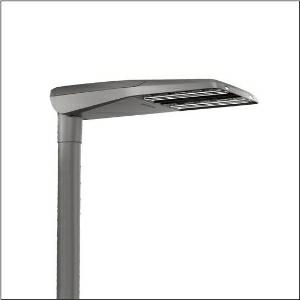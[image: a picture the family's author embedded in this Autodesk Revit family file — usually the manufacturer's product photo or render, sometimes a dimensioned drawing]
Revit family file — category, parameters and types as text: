
# Revit family: streetlight_sl_11_iq_midi___st1_2a_5xc3a61g08me_c756
name_source: partatom
category: Lighting Fixtures
units: mm (PartAtom-declared; Revit-internal decimal feet)

## family parameters
Cut with Voids When Loaded = No
Host = Face
Light Source = No
Part Type = Normal
Room Calculation Point = No
Round Connector Dimension = Use Diameter
Shared = No

## types (1)
- --- (1 x LED, 16120 lm, 123.9 W, 2700K)
    Apparent Load = 124 VA
    CIE Flux Codes = 32 70 96 100 100
    Color Rendering = 70
    Color Temperature = 2700K
    Default Elevation = 1800 mm
    Description = Streetlight SL 11 iQ midi, mast luminaire, primary light control with 3 zone facetted reflector, of plastic, silver coated, highly specular, primary optical cover: cover, of PMMA, transparent, light distribution: ST1.2a, light emission: direct distribution, primary light characteristic: asymmetric, installation type: post-top, side-entry, lamps: LED, High Power LED, rated values: 16.120lm | 123,9W | 130,1lm/W (begin service life); end service life: 16.120lm | 130,9W; at 50% lumin. flux: 8.060lm | 56,7W | 142,2lm/W, colour temperature: 2700K, colour rendering: CRI > 70, light colour: 727, light setting 1 begin service life: 100% | 16.120lm | 123,9W | 130,1lm/W | 2.700K, light setting 1 end service life: 130,9W, further light settings possible, control: Street-Remote, Auto-Match, Temp-Guard, Lumen-Switch, Night-Set, Smart-Wire, Light-Fading, Desk-Remote (wireless, voltage-free reading and setting of iQ features in the workshop via application-optimized NFC function/RFID function), optimised constant luminous flux control (CLO 2.0), pre-setting: linear dimming characteristic, with cable H07RN-F 5x 1.5mm², mains connection: 230..240V, AC, 50/60Hz, connection cable pre-assembled, cable length: 12,5m, luminaire housing, of diecast aluminium, powder-coated, SITECO metallic grey (DB 702S), please order mast flange separately, inclination adjustable without tools: 0°, 5°, 10°, 15° (post-top) | 0°, -5°, -10°, -15° (side-entry), sealing non-destructively replaceable, multi-level sealing system, length: 780mm, width: 376mm, height: 118mm, mast flange for spigot size: 42mm (side-entry): 5XC10008XM4, 60/48mm (side-entry/post-top): 5XC10108XM2, 76/60mm (side-entry/post-top): 5XC10108XM1, equipment: Power, protection rating (complete): IP66, insulation class (complete): insulation class II (safety insulation), certification: CE, ENEC, ENEC+, VDE, impact resistance: IK10, permissible operating ambient temperature for outdoor applications: -25..+50°C, standard-compliant lighting for roads and squares, Environmental Product Declaration (EPD) tested and certified by an independent institute, packaging unit: 1 piece

Light Distribution: ST1.2a
    Height = 118 mm
    Lamp = 1 x LED
    Lamp Light Flux = 16120 lm
    Lamp Power = 123.9 W
    Lamp count = 1
    Length = 780 mm
    Luminous efficacy = 130 lm/W
    Manufacturer = Siteco
    ModVariant = No
    Model = 5XC3A61G08ME
    Number of Poles = 1
    OnlyDefault = Yes
    Power Factor = 1
    Product Name = Streetlight SL 11 iQ midi | ST1.2a
    Product group = mast luminaire | pylon top
    ProductGroupID = 6100
    Protection Class = Protection class II
    Protection Degree = IP 66
    RLX_Detail_Level = 1
    RLX_Emergency_Light_Flux = 0 lm
    RLX_Emergency_Type = 0
    RLX_Emergency_Type_DB = No
    RlxData = <blob elided: 71013 chars, md5=b5ebc1dd>
    Socket = socket
    Standby Power = 0 W
    System Light Flux = 16119 lm
    System Power = 124 W
    Type Comments = factory setting: luminous flux: 100 % | dim-lin: 254 | 554 mA
    Type Image = l_1005960.jpg
    URL = http://relux.com
    VarID = @adj_085997
    Voltage = 0 V
    Weight = 0.00 kg
    Width = 376 mm

## geometry (parser evidence)
native form markers: Blend x4, Sweep x9
no freeform markers — native parametric forms only
